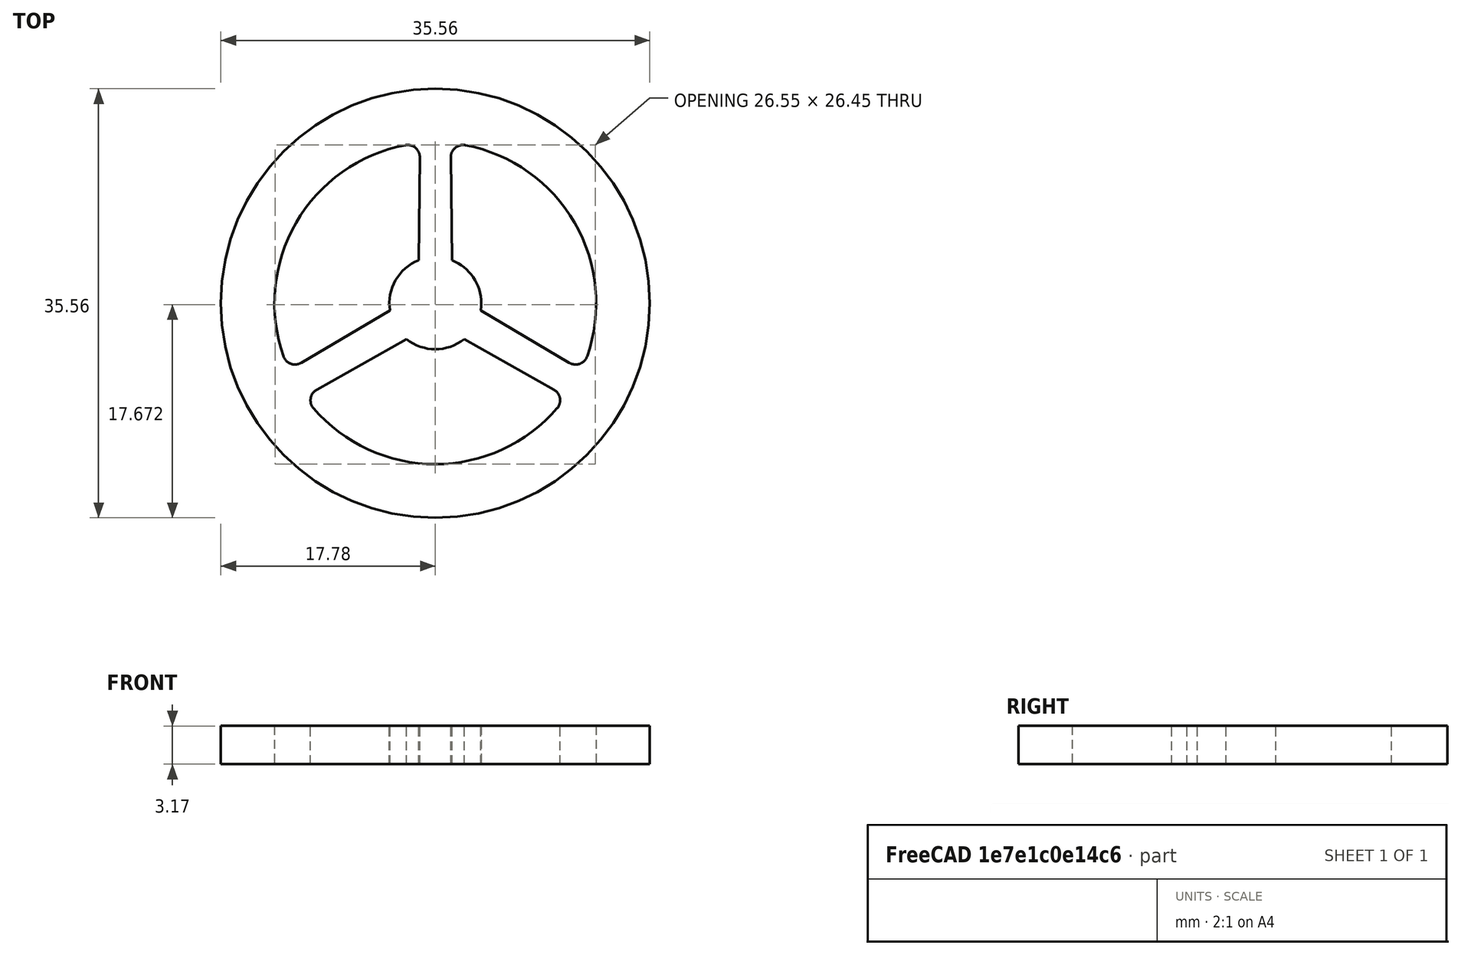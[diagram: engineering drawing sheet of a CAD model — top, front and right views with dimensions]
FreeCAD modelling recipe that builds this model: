
FCSTD DOCUMENT  (FreeCAD 0.21R30747 (Git))
Label: Driver_Template
License: All rights reserved
LicenseURL: http://en.wikipedia.org/wiki/All_rights_reserved
objects: Sketcher::SketchObject×2, PartDesign::Pad×2, TechDraw::DrawViewDimExtent×2, TechDraw::DrawSVGTemplate×1, PartDesign::Fillet×1, PartDesign::Body×1, TechDraw::DrawProjGroupItem×1, TechDraw::DrawProjGroup×1, TechDraw::DrawPage×1
note: 9 computed .brp shape members not serialized (recipe doc carries the construction recipe); baked Part::Feature solids carry a one-line shape summary decoded from their .brp

FEATURE [Sketcher::SketchObject] Sketch
  FullyConstrained = true
  MapMode = 5
  Support = -> [XY_Plane]
  sketch-geometry (22):
    g0: Circle CenterX=0 CenterY=0 CenterZ=0 NormalX=0 NormalY=0 NormalZ=1 AngleXU=0 Radius=17.78
    g1: LineSegment StartX=-1.27 StartY=13.2744 StartZ=0 EndX=-1.39467 EndY=1.88415 EndZ=0
    g2: LineSegment StartX=-2.32906 StartY=0.265745 StartZ=0 EndX=-12.131 EndY=-5.53734 EndZ=0
    g3: LineSegment StartX=1.27 StartY=13.2744 StartZ=0 EndX=1.39467 EndY=1.88415 EndZ=0
    g4: LineSegment StartX=2.32906 StartY=0.265745 StartZ=0 EndX=12.131 EndY=-5.53734 EndZ=0
    g5: LineSegment StartX=-0.934387 StartY=-2.1499 StartZ=0 EndX=-10.861 EndY=-7.73705 EndZ=0
    g6: LineSegment StartX=0.934387 StartY=-2.1499 StartZ=0 EndX=10.861 EndY=-7.73705 EndZ=0
    g7: ArcOfCircle CenterX=3.29956 CenterY=1.905 CenterZ=0 NormalX=0 NormalY=0 NormalZ=1 AngleXU=0 Radius=1.905 StartAngle=3.15254 EndAngle=4.17785
    g8: ArcOfCircle CenterX=-3.29956 CenterY=1.905 CenterZ=0 NormalX=0 NormalY=0 NormalZ=1 AngleXU=0 Radius=1.905 StartAngle=5.24693 EndAngle=6.27224
    g9: ArcOfCircle CenterX=0 CenterY=-3.81 CenterZ=0 NormalX=0 NormalY=0 NormalZ=1 AngleXU=0 Radius=1.905 StartAngle=1.05814 EndAngle=2.08345
    g10: ArcOfCircle CenterX=0 CenterY=0 CenterZ=0 NormalX=0 NormalY=0 NormalZ=1 AngleXU=0 Radius=13.335 StartAngle=1.66618 EndAngle=3.56981
    g11: ArcOfCircle CenterX=0 CenterY=0 CenterZ=0 NormalX=0 NormalY=0 NormalZ=1 AngleXU=0 Radius=13.335 StartAngle=5.85497 EndAngle=7.7586
    g12: ArcOfCircle CenterX=0 CenterY=0 CenterZ=0 NormalX=0 NormalY=0 NormalZ=1 AngleXU=0 Radius=13.335 StartAngle=3.76057 EndAngle=5.6642
    g13: LineSegment StartX=-3.29956 StartY=1.905 StartZ=0 EndX=0 EndY=0 EndZ=0
    g14: LineSegment StartX=0 StartY=-3.81 StartZ=0 EndX=0 EndY=0 EndZ=0
    g15: LineSegment StartX=0 StartY=0 StartZ=0 EndX=3.29956 EndY=1.905 EndZ=0
    g16: LineSegment StartX=3.29956 StartY=1.905 StartZ=0 EndX=0 EndY=-3.81 EndZ=0
    g17: LineSegment StartX=0 StartY=-3.81 StartZ=0 EndX=-3.29956 EndY=1.905 EndZ=0
    g18: LineSegment StartX=-3.29956 StartY=1.905 StartZ=0 EndX=3.29956 EndY=1.905 EndZ=0
    g19: LineSegment StartX=12.131 StartY=-5.53734 StartZ=0 EndX=10.861 EndY=-7.73705 EndZ=0
    g20: LineSegment StartX=-1.27 StartY=13.2744 StartZ=0 EndX=1.27 EndY=13.2744 EndZ=0
    g21: LineSegment StartX=-12.131 StartY=-5.53734 StartZ=0 EndX=-10.861 EndY=-7.73705 EndZ=0
  constraints (53):
    c: Coincident(g0,g-1)
    c: Diameter(g0) = 35.56
    c: Tangent(g3,g7) = -1.5708
    c: Tangent(g4,g7) = -1.5708
    c: Tangent(g2,g8) = 1.5708
    c: Tangent(g1,g8) = 1.5708
    c: Tangent(g5,g9) = -1.5708
    c: Tangent(g6,g9) = 1.5708
    c: Coincident(g10,g0)
    c: Coincident(g10,g2)
    c: Coincident(g10,g1)
    c: Coincident(g11,g0)
    c: Coincident(g11,g3)
    c: Coincident(g11,g4)
    c: Coincident(g12,g0)
    c: Coincident(g12,g6)
    c: Coincident(g12,g5)
    c: Equal(g5,g6)
    c: Equal(g6,g4)
    c: Equal(g4,g3)
    c: Equal(g3,g1)
    c: Equal(g1,g2)
    c: Equal(g8,g7)
    c: Equal(g7,g9)
    c: Coincident(g13,g8)
    c: Coincident(g13,g0)
    c: Coincident(g14,g9)
    c: Coincident(g14,g0)
    c: Vertical(g14)
    c: Coincident(g15,g0)
    c: Coincident(g15,g7)
    c: Coincident(g16,g7)
    c: Coincident(g16,g9)
    c: Coincident(g17,g9)
    c: Coincident(g17,g8)
    c: Coincident(g18,g8)
    c: Coincident(g18,g7)
    c: Horizontal(g18)
    c: Equal(g18,g16)
    c: Equal(g16,g17)
    c: Equal(g14,g13)
    c: Distance(g13) = 3.81
    c: Diameter(g8) = 3.81
    c: Coincident(g19,g4)
    c: Coincident(g19,g6)
    c: Coincident(g20,g1)
    c: Coincident(g20,g3)
    c: Coincident(g21,g2)
    c: Coincident(g21,g5)
    c: Equal(g19,g20)
    c: Equal(g20,g21)
    c: Distance(g19) = 2.54
    c: Diameter(g10) = 26.67
FEATURE [PartDesign::Pad] Pad
  Direction = (0,0,1)
  Length = 3.175
  Length2 = 100.076
  Profile = -> Sketch
  ReferenceAxis = -> Sketch [N_Axis]
  Type = 0
FEATURE [TechDraw::DrawSVGTemplate] Template
  EditableTexts = Designed_by_Name=Design by Matthew; Drawing_number=a3baa059; FC-Date=Dec 2021; FC-SC=1:1; FC-SH=1 of 1; FC-Title=Driver Patch; Subtitle=Tidal Force Robotics; Weight=0.01
  Height = 210
  Orientation = 1
  Width = 297
FEATURE [PartDesign::Fillet] Fillet
  Base = -> Pad [Edge23,Edge16,Edge29,Edge8,Edge5,Edge28]
  BaseFeature = -> Pad
  Radius = 1.016
  SupportTransform = false
  UseAllEdges = false
FEATURE [Sketcher::SketchObject] Sketch001
  FullyConstrained = true
  MapMode = 5
  Placement = pos=(0,0,3.175) rot=(0,0,1;0rad)
  Support = -> [Fillet]
  sketch-geometry (1):
    g0: Circle CenterX=0 CenterY=0 CenterZ=0 NormalX=0 NormalY=0 NormalZ=1 AngleXU=0 Radius=3.81
  constraints (2):
    c: Coincident(g0,g-1)
    c: Diameter(g0) = 7.62
FEATURE [PartDesign::Pad] Pad001
  BaseFeature = -> Fillet
  Direction = (0,0,1)
  Length = 9.906
  Length2 = 100.076
  Profile = -> Sketch001
  ReferenceAxis = -> Sketch001 [N_Axis]
  Type = 3
  UpToFace = -> Fillet [Face2]
FEATURE [PartDesign::Body] Body  label="Driver Template Body"
  Group = -> [Sketch,Pad,Fillet,Sketch001,Pad001]
  Origin = -> Origin
  Tip = -> Pad001
FEATURE [TechDraw::DrawProjGroupItem] ProjItem  label="Front"
  CoarseView = false
  Direction = (0,0,1)
  Focus = 100
  HardHidden = false
  IsoCount = 0
  IsoHidden = false
  IsoVisible = false
  LockPosition = true
  Perspective = false
  Rotation = 0
  RotationVector = (1,0,0)
  ScaleType = 2
  SeamHidden = false
  SeamVisible = true
  SmoothHidden = false
  SmoothVisible = true
  Source = -> [Body]
  Type = 0
  X = 0
  XDirection = (1,0,0)
  Y = 0
FEATURE [TechDraw::DrawProjGroup] ProjGroup
  Anchor = -> ProjItem
  AutoDistribute = true
  LockPosition = false
  ProjectionType = 0
  Rotation = 0
  ScaleType = 0
  Source = -> [Body]
  Views = -> [ProjItem]
  X = 148.5
  Y = 105
  spacingX = 14.986
  spacingY = 14.986
FEATURE [TechDraw::DrawViewDimExtent] DimExtent
  AngleOverride = false
  Arbitrary = false
  ArbitraryTolerances = false
  CosmeticTags = 4876a07e-5734-4a42-9c70-3ad1e6a7d9bc | d5695a1d-5df9-4573-af45-24d7c8faea45
  DirExtent = 0
  EqualTolerance = true
  ExtensionAngle = 0
  FormatSpec = %.3f
  FormatSpecOverTolerance = %+.3f
  FormatSpecUnderTolerance = %+.3f
  Inverted = false
  LineAngle = 0
  LockPosition = false
  MeasureType = 1
  OverTolerance = 0
  References2D = -> [ProjItem]
  Rotation = 0
  ScaleType = 0
  Source = -> [ProjItem]
  TheoreticalExact = false
  Type = 1
  UnderTolerance = 0
  X = 0.802663
  Y = -28.3225
FEATURE [TechDraw::DrawViewDimExtent] DimExtent001
  AngleOverride = false
  Arbitrary = false
  ArbitraryTolerances = false
  CosmeticTags = cb7f4163-6724-4b0a-a852-f6ca696e9f43 | 79479888-a2d5-4abe-9f57-d4747772a0c1
  DirExtent = 1
  EqualTolerance = true
  ExtensionAngle = 0
  FormatSpec = %.3f
  FormatSpecOverTolerance = %+.3f
  FormatSpecUnderTolerance = %+.3f
  Inverted = false
  LineAngle = 0
  LockPosition = false
  MeasureType = 1
  OverTolerance = 0
  References2D = -> [ProjItem]
  Rotation = 0
  ScaleType = 0
  Source = -> [ProjItem]
  TheoreticalExact = false
  Type = 2
  UnderTolerance = 0
  X = 31.3039
  Y = 1.83466
FEATURE [TechDraw::DrawPage] Page
  KeepUpdated = true
  NextBalloonIndex = 1
  ProjectionType = 0
  Template = -> Template
  Views = -> [ProjGroup,DimExtent,DimExtent001]
